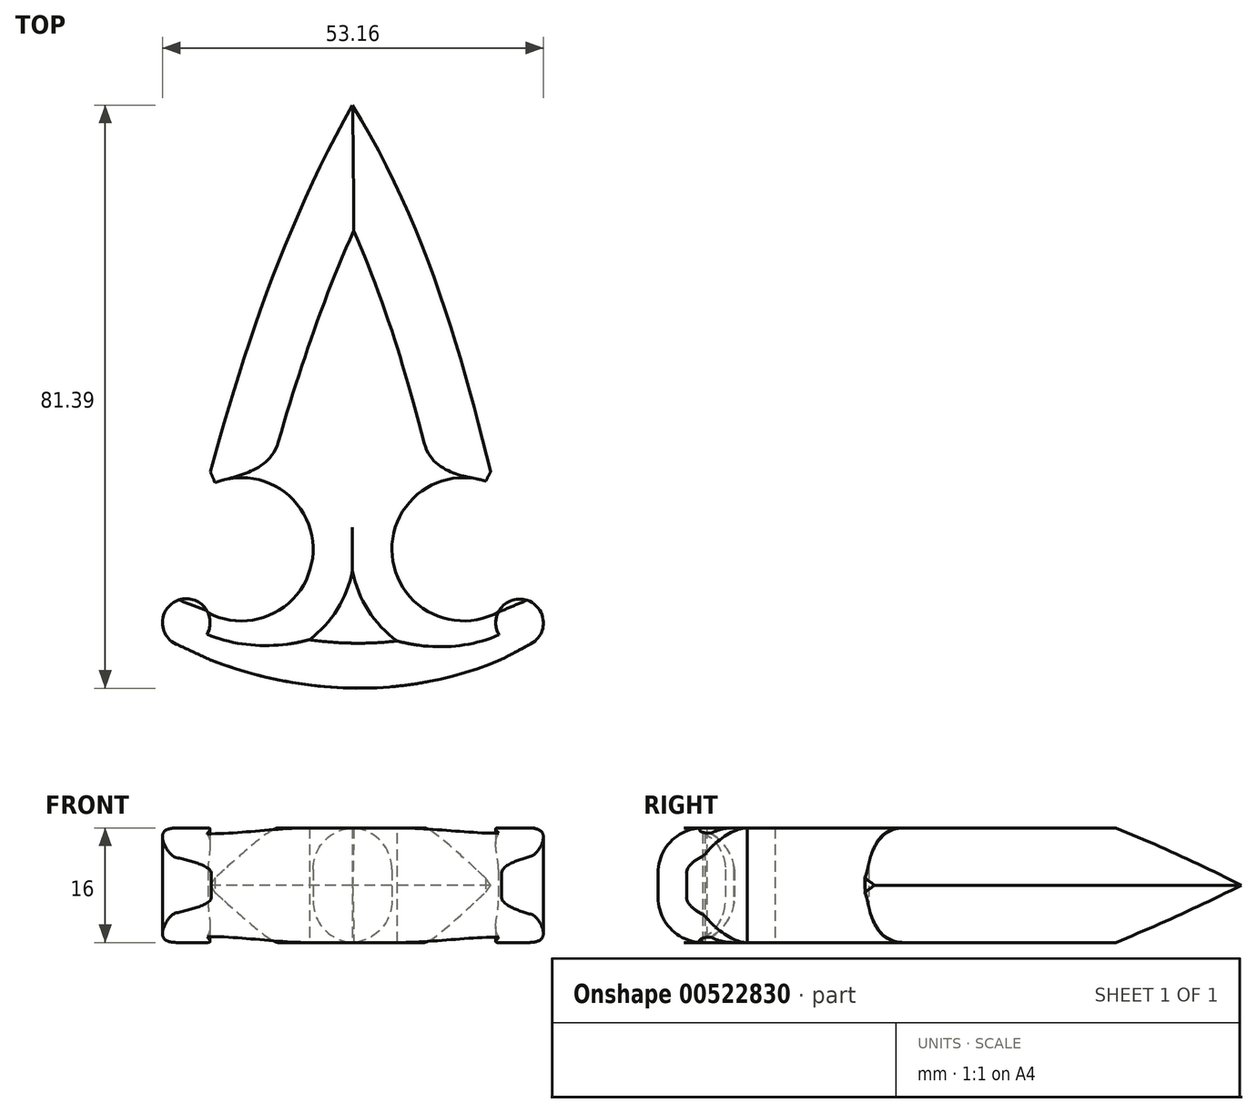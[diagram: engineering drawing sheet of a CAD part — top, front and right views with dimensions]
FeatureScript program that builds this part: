
annotation { "Feature Type Name" : "Feature", "Feature Type Description" : "" }
export const myFeature = defineFeature(function(context is Context, id is Id, definition is map)
    precondition{}
    {
        {
            var Q0;
            Q0=qCreatedBy(makeId("Top.planeOp"),FACE);
            var sketch = newSketch(context, id + "F0", { "sketchPlane" : qUnion([Q0])});
            skCircle(sketch, "E0", {"center": v(-19.88, 0) * mm, "radius": 10 * mm});
            skCircle(sketch, "E1", {"center": v(11.12, 0) * mm, "radius": 10 * mm});
            skLineSegment(sketch, "E2", {"start": v(14.9, 10.84) * mm, "end": v(-24.2, 10.84) * mm});
            skFitSpline(sketch, "E3", {"points": [v(-4.38, 62) * mm, v(-24.2, 10.84) * mm], "startDerivative": vector(-28.01, -49.81) * mm, "endDerivative": vector(-14.31, -52.28) * mm});
            skFitSpline(sketch, "E4", {"points": [v(-4.38, 62) * mm, v(14.9, 10.84) * mm], "startDerivative": vector(30.54, -49.81) * mm, "endDerivative": vector(12.7, -51.03) * mm});
            skCircle(sketch, "E5", {"center": v(-27.57, -10.22) * mm, "radius": 3.32 * mm});
            skCircle(sketch, "E6", {"center": v(18.95, -10.27) * mm, "radius": 3.32 * mm});
            skFitSpline(sketch, "E7", {"points": [v(-24.55, -8.84) * mm, v(16, -8.73) * mm], "startDerivative": vector(40.05, -15.18) * mm, "endDerivative": vector(39.47, 16.46) * mm});
            skFitSpline(sketch, "E8", {"points": [v(-24.1, -15.49) * mm, v(16.45, -15.38) * mm], "startDerivative": vector(40.05, -15.18) * mm, "endDerivative": vector(39.47, 16.46) * mm});
            skLineSegment(sketch, "E9", {"start": v(-24.1, -15.49) * mm, "end": v(-28.96, -13.24) * mm});
            skLineSegment(sketch, "E10", {"start": v(16.45, -15.38) * mm, "end": v(20.52, -13.2) * mm});
            skLineSegment(sketch, "E11", {"start": v(-24.2, 10.84) * mm, "end": v(-23.56, 9.3) * mm});
            skLineSegment(sketch, "E12", {"start": v(14.9, 10.84) * mm, "end": v(14.23, 9.5) * mm});
            skSolve(sketch);
        }
        {
            var Q0;
            {var subQ0=sQuery(id+"F0.wireOp",EDGE,"E5");var subQ1=sQuery(id+"F0.wireOp",EDGE,"E0");var subQ3=makeQuery(id+"F0.imprint","INTERSECT",VERTEX,{"derivedFrom":[subQ1,subQ0]});Q0=makeQuery(id+"F0.imprint","IMPRINT",FACE,{"disambiguationData":[TD([[makeQuery(id+"F0.imprint","IMPRINT",EDGE,{"disambiguationData":[TD([[subQ3,-1.0]])],"derivedFrom":subQ1}),1.0]])]});}
            var Q1;
            {var subQ0=sQuery(id+"F0.wireOp",EDGE,"E5");var subQ4=makeQuery(id+"F0.imprint","INTERSECT",VERTEX,{"derivedFrom":[subQ0,sQuery(id+"F0.wireOp",EDGE,"E9")]});Q1=makeQuery(id+"F0.imprint","IMPRINT",FACE,{"disambiguationData":[TD([[makeQuery(id+"F0.imprint","IMPRINT",EDGE,{"disambiguationData":[TD([[subQ4,1.0]])],"derivedFrom":subQ0}),1.0]])]});}
            var Q2;
            {var subQ0=sQuery(id+"F0.wireOp",EDGE,"E6");var subQ1=sQuery(id+"F0.wireOp",EDGE,"E1");var subQ3=makeQuery(id+"F0.imprint","INTERSECT",VERTEX,{"derivedFrom":[subQ1,subQ0]});Q2=makeQuery(id+"F0.imprint","IMPRINT",FACE,{"disambiguationData":[TD([[makeQuery(id+"F0.imprint","IMPRINT",EDGE,{"disambiguationData":[TD([[subQ3,1.0]])],"derivedFrom":subQ1}),1.0]])]});}
            var Q3;
            {var subQ0=sQuery(id+"F0.wireOp",EDGE,"E6");var subQ4=makeQuery(id+"F0.imprint","INTERSECT",VERTEX,{"derivedFrom":[subQ0,sQuery(id+"F0.wireOp",EDGE,"E10")]});Q3=makeQuery(id+"F0.imprint","IMPRINT",FACE,{"disambiguationData":[TD([[makeQuery(id+"F0.imprint","IMPRINT",EDGE,{"disambiguationData":[TD([[subQ4,-1.0]])],"derivedFrom":subQ0}),1.0]])]});}
            var Q4;
            Q4=makeQuery(id+"F0.imprint","IMPRINT",FACE,{"disambiguationData":[TD([[makeQuery(id+"F0.imprint","IMPRINT",EDGE,{"derivedFrom":sQuery(id+"F0.wireOp",EDGE,"E2")}),1.0]])]});
            var Q5;
            Q5=makeQuery(id+"F0.imprint","IMPRINT",FACE,{"disambiguationData":[TD([[makeQuery(id+"F0.imprint","IMPRINT",EDGE,{"derivedFrom":sQuery(id+"F0.wireOp",EDGE,"E8")}),1.0]])]});
            var Q6;
            Q6=makeQuery(id+"F0.imprint","IMPRINT",FACE,{"disambiguationData":[TD([[makeQuery(id+"F0.imprint","IMPRINT",EDGE,{"derivedFrom":sQuery(id+"F0.wireOp",EDGE,"E2")}),-1.0]])]});
            extrude(context, id + "F1", {"entities" : qUnion([Q0, Q1, Q2, Q3, Q4, Q5, Q6]), "depth" : 16 * mm, "offsetDistance" : 25 * mm});
        }
        {
            var Q0;
            Q0=makeQuery(id+"F1.opExtrude","CAP_EDGE",EDGE,{"disambiguationData":[OSD([sQuery(id+"F0.wireOp",EDGE,"E0")])],"isStart":false});
            var Q1;
            Q1=makeQuery(id+"F1.opExtrude","CAP_EDGE",EDGE,{"disambiguationData":[OSD([sQuery(id+"F0.wireOp",EDGE,"E0")])],"isStart":true});
            var Q2;
            Q2=makeQuery(id+"F1.opExtrude","CAP_EDGE",EDGE,{"disambiguationData":[OSD([sQuery(id+"F0.wireOp",EDGE,"E1")])],"isStart":true});
            var Q3;
            Q3=makeQuery(id+"F1.opExtrude","CAP_EDGE",EDGE,{"disambiguationData":[OSD([sQuery(id+"F0.wireOp",EDGE,"E1")])],"isStart":false});
            fillet(context, id + "F2", {"entities" : qUnion([Q0, Q1, Q2, Q3]), "radius" : 5.8 * mm, "tangentPropagation" : true, "allowEdgeOverflow" : false});
        }
        {
            var Q0;
            Q0=makeQuery(id+"F1.opExtrude","CAP_EDGE",EDGE,{"disambiguationData":[OSD([sQuery(id+"F0.wireOp",EDGE,"E4")])],"isStart":true});
            var Q1;
            Q1=makeQuery(id+"F1.opExtrude","CAP_EDGE",EDGE,{"disambiguationData":[OSD([sQuery(id+"F0.wireOp",EDGE,"E4")])],"isStart":false});
            var Q2;
            Q2=makeQuery(id+"F1.opExtrude","CAP_EDGE",EDGE,{"disambiguationData":[OSD([sQuery(id+"F0.wireOp",EDGE,"E3")])],"isStart":false});
            var Q3;
            Q3=makeQuery(id+"F1.opExtrude","CAP_EDGE",EDGE,{"disambiguationData":[OSD([sQuery(id+"F0.wireOp",EDGE,"E3")])],"isStart":true});
            chamfer(context, id + "F3", {"entities" : qUnion([Q0, Q1, Q2, Q3]), "width" : 8 * mm, "tangentPropagation" : true});
        }
        {
            var Q0;
            Q0=makeQuery(id+"F1.opExtrude","CAP_EDGE",EDGE,{"disambiguationData":[OSD([sQuery(id+"F0.wireOp",EDGE,"E8")])],"isStart":false});
            var Q1;
            Q1=makeQuery(id+"F1.opExtrude","CAP_EDGE",EDGE,{"disambiguationData":[OSD([sQuery(id+"F0.wireOp",EDGE,"E8")])],"isStart":true});
            fillet(context, id + "F4", {"entities" : qUnion([Q0, Q1]), "radius" : 6.28 * mm, "tangentPropagation" : true, "allowEdgeOverflow" : false});
        }
        {
            var Q0;
            Q0=makeQuery(id+"F4.opFillet","SPLIT",FACE,{"disambiguationData":[OD(2.0)],"derivedFrom":makeQuery(id+"F2.opFillet","SPLIT",FACE,{"disambiguationData":[OD(0.0)],"derivedFrom":makeQuery(id+"F1.opExtrude","CAP_FACE",FACE,{"disambiguationData":[OSD([sQuery(id+"F0.wireOp",EDGE,"E0"),sQuery(id+"F0.wireOp",EDGE,"E1"),sQuery(id+"F0.wireOp",EDGE,"E3"),sQuery(id+"F0.wireOp",EDGE,"E4"),sQuery(id+"F0.wireOp",EDGE,"E5"),sQuery(id+"F0.wireOp",EDGE,"E6"),sQuery(id+"F0.wireOp",EDGE,"E8"),sQuery(id+"F0.wireOp",EDGE,"E9"),sQuery(id+"F0.wireOp",EDGE,"E10"),sQuery(id+"F0.wireOp",EDGE,"E11"),sQuery(id+"F0.wireOp",EDGE,"E12")])],"isStart":true})})});
            extrude(context, id + "F5", {"entities" : qUnion([Q0]), "operationType" : NewBodyOperationType.REMOVE, "oppositeDirection" : true, "depth" : 25 * mm, "offsetDistance" : 25 * mm});
        }
    });
